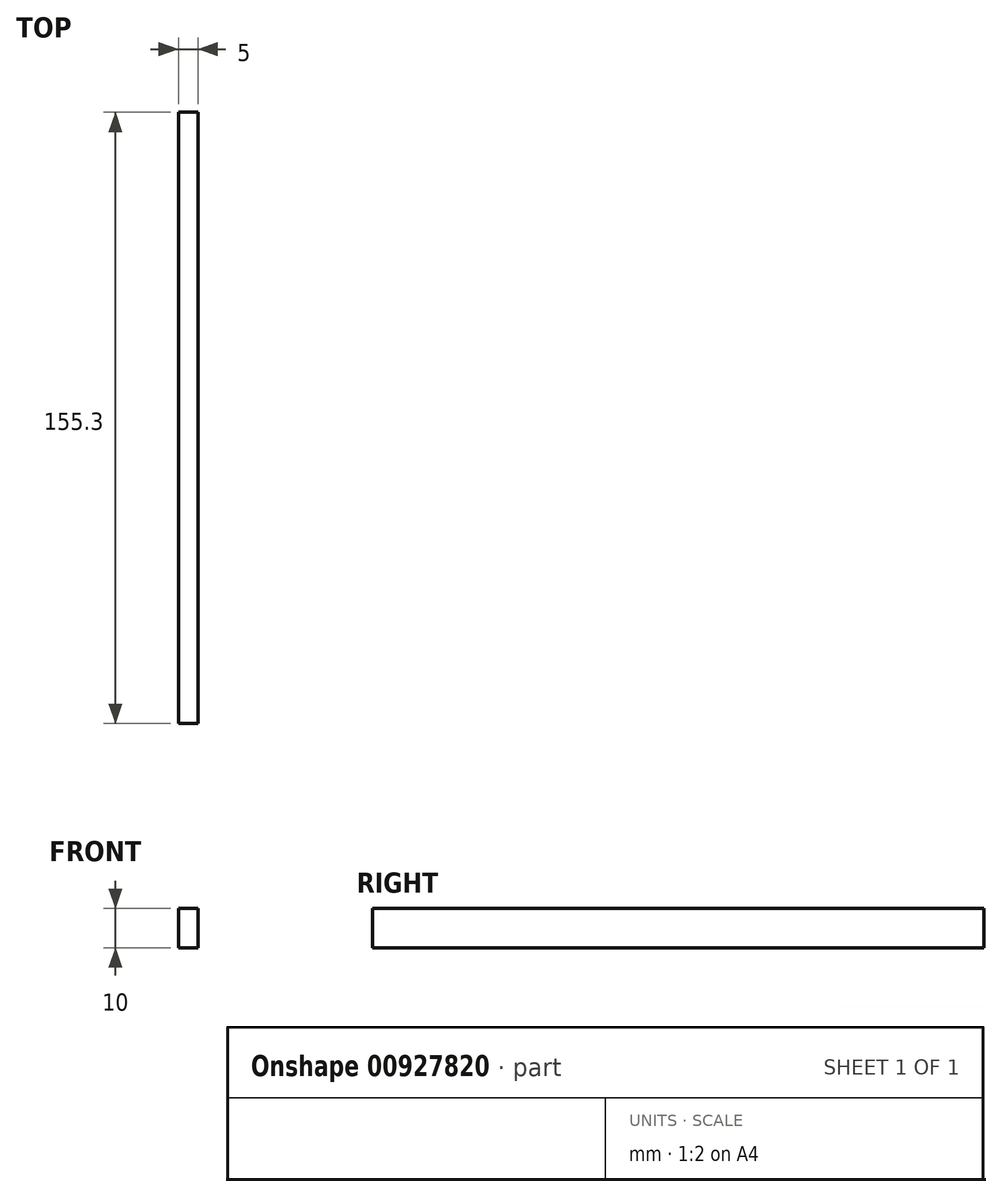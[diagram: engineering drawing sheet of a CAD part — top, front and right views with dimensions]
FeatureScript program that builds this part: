
annotation { "Feature Type Name" : "Feature", "Feature Type Description" : "" }
export const myFeature = defineFeature(function(context is Context, id is Id, definition is map)
    precondition{}
    {
        {
            var Q0;
            Q0=qCreatedBy(makeId("Front.planeOp"),FACE);
            var sketch = newSketch(context, id + "F0", { "sketchPlane" : qUnion([Q0])});
            skLineSegment(sketch, "E0.bottom", {"start": v(2.5, 5) * mm, "end": v(-2.5, 5) * mm});
            skLineSegment(sketch, "E0.top", {"start": v(2.5, -5) * mm, "end": v(-2.5, -5) * mm});
            skLineSegment(sketch, "E0.left", {"start": v(2.5, 5) * mm, "end": v(2.5, -5) * mm});
            skLineSegment(sketch, "E0.right", {"start": v(-2.5, 5) * mm, "end": v(-2.5, -5) * mm});
            skPoint(sketch, "E0.middle", {"position": v(0, 0) * mm});
            skSolve(sketch);
        }
        {
            var Q0;
            Q0=qSketchRegion(id+"F0",true);
            extrude(context, id + "F1", {"entities" : qUnion([Q0]), "depth" : 155.3 * mm, "offsetDistance" : 25 * mm});
        }
    });
